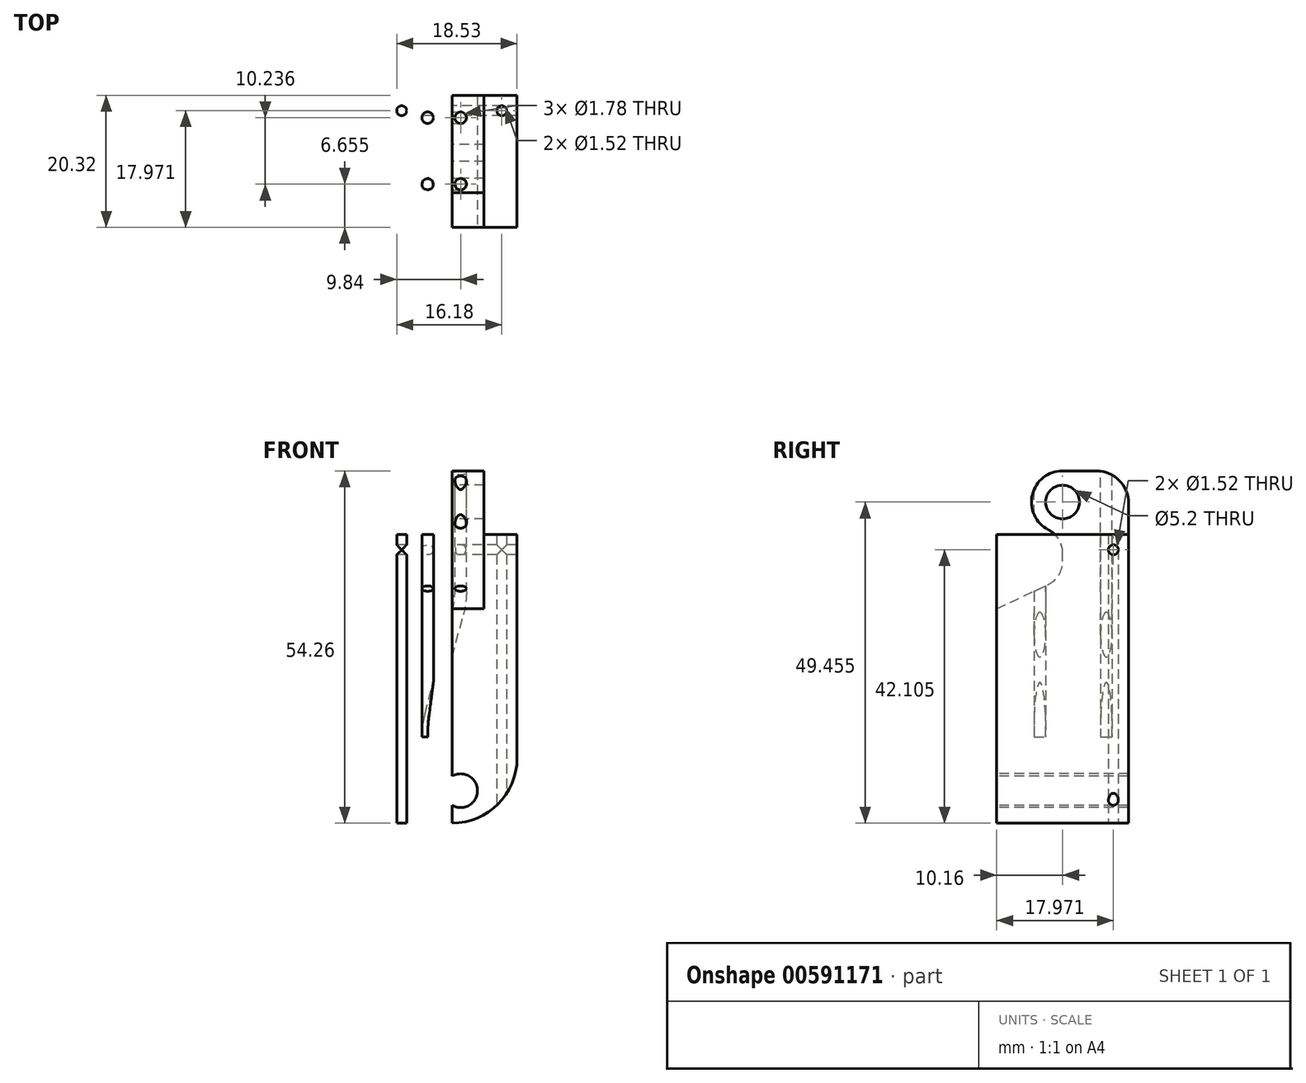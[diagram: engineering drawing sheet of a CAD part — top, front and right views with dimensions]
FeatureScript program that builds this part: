
annotation { "Feature Type Name" : "Feature", "Feature Type Description" : "" }
export const myFeature = defineFeature(function(context is Context, id is Id, definition is map)
    precondition{}
    {
        {
            var Q0;
            Q0=qCreatedBy(makeId("Front.planeOp"),FACE);
            var sketch = newSketch(context, id + "F0", { "sketchPlane" : qUnion([Q0])});
            skLineSegment(sketch, "E0.bottom", {"start": v(11.43, 22.23) * mm, "end": v(3.61, 22.23) * mm});
            skLineSegment(sketch, "E0.left", {"start": v(11.43, 22.23) * mm, "end": v(11.43, -22.22) * mm});
            skLineSegment(sketch, "E0.right", {"start": v(-11.43, 22.23) * mm, "end": v(-11.43, -22.23) * mm});
            skPoint(sketch, "E0.middle", {"position": v(0, 0) * mm});
            skLineSegment(sketch, "E1.trimOffspring", {"start": v(11.43, -22.22) * mm, "end": v(-11.43, -22.22) * mm});
            skLineSegment(sketch, "E2.bottom", {"start": v(3.61, 32.03) * mm, "end": v(-3.61, 32.03) * mm});
            skLineSegment(sketch, "E2.left", {"start": v(3.61, 32.03) * mm, "end": v(3.61, 22.23) * mm});
            skLineSegment(sketch, "E2.right", {"start": v(-3.61, 32.03) * mm, "end": v(-3.61, 22.23) * mm});
            skPoint(sketch, "E2.middle", {"position": v(0, 22.23) * mm});
            skLineSegment(sketch, "E3.trimOffspring", {"start": v(-3.61, 22.23) * mm, "end": v(-11.43, 22.23) * mm});
            skPoint(sketch, "E4.orphan", {"position": v(-3.61, 12.43) * mm});
            skPoint(sketch, "E5.orphan", {"position": v(3.61, 12.43) * mm});
            skLineSegment(sketch, "E6", {"start": v(8.7, -22.23) * mm, "end": v(8.7, 22.23) * mm});
            skSolve(sketch);
        }
        {
            var Q0;
            {var subQ1=sQuery(id+"F0.wireOp",EDGE,"E0.right");Q0=makeQuery(id+"F0.imprint","IMPRINT",FACE,{"disambiguationData":[TD([[makeQuery(id+"F0.imprint","IMPRINT",EDGE,{"derivedFrom":subQ1}),1.0]])]});}
            extrude(context, id + "F1", {"entities" : qUnion([Q0]), "depth" : 20.32 * mm, "offsetDistance" : 25.4 * mm, "symmetric" : true});
        }
        {
            var Q0;
            Q0=makeQuery(id+"F1.opExtrude","SWEPT_FACE",FACE,{"disambiguationData":[OSD([sQuery(id+"F0.wireOp",EDGE,"E0.right")])]});
            var sketch = newSketch(context, id + "F2", { "sketchPlane" : qUnion([Q0])});
            skLineSegment(sketch, "E7", {"start": v(10.16, 22.23) * mm, "end": v(-5.46, 22.23) * mm});
            skLineSegment(sketch, "E8", {"start": v(10.16, 22.23) * mm, "end": v(10.16, 10.8) * mm});
            skLineSegment(sketch, "E9", {"start": v(10.16, 10.8) * mm, "end": v(-0.57, 15.8) * mm});
            skPoint(sketch, "E10.visualSharp", {"position": v(-2.14, 14.35) * mm});
            skArc(sketch, "E10.filletArc", {"start": v(-5.46, 22.23) * mm, "mid": v(-3.7, 18.5) * mm, "end": v(-0.57, 15.8) * mm});
            skSolve(sketch);
        }
        {
            var Q0;
            Q0=makeQuery(id+"F2.imprint","IMPRINT",FACE,{"disambiguationData":[TD([[makeQuery(id+"F2.imprint","IMPRINT",EDGE,{"derivedFrom":sQuery(id+"F2.wireOp",EDGE,"E7")}),1.0]])]});
            var Q1;
            Q1=makeQuery(id+"F1.opExtrude","SWEPT_FACE",FACE,{"disambiguationData":[OSD([sQuery(id+"F0.wireOp",EDGE,"E2.right")])]});
            extrude(context, id + "F3", {"entities" : qUnion([Q0]), "operationType" : NewBodyOperationType.REMOVE, "oppositeDirection" : true, "depth" : 7.82 * mm, "endBoundEntityFace" : qUnion([Q1]), "offsetDistance" : 25.4 * mm});
        }
        {
            var Q0;
            Q0=makeQuery(id+"F3.boolean.opBoolean","MERGE",FACE,{"derivedFrom":[makeQuery(id+"F1.opExtrude","SWEPT_FACE",FACE,{"disambiguationData":[OSD([sQuery(id+"F0.wireOp",EDGE,"E2.right")])]}),makeQuery(id+"F3.opExtrude","CAP_FACE",FACE,{"disambiguationData":[OSD([sQuery(id+"F2.wireOp",EDGE,"E7"),sQuery(id+"F2.wireOp",EDGE,"E8"),sQuery(id+"F2.wireOp",EDGE,"E9"),sQuery(id+"F2.wireOp",EDGE,"E10.filletArc")])],"isStart":false})]});
            var sketch = newSketch(context, id + "F4", { "sketchPlane" : qUnion([Q0])});
            skLineSegment(sketch, "E11", {"start": v(0, 22.23) * mm, "end": v(0, 22.42) * mm});
            skCircle(sketch, "E12", {"center": v(0, 27.22) * mm, "radius": 2.6 * mm});
            skArc(sketch, "E13", {"start": v(0, 22.42) * mm, "mid": v(4.8, 27.22) * mm, "end": v(0, 32.03) * mm});
            skLineSegment(sketch, "E14", {"start": v(0, 32.03) * mm, "end": v(10.16, 32.03) * mm});
            skLineSegment(sketch, "E15", {"start": v(10.16, 32.03) * mm, "end": v(10.16, 10.8) * mm});
            skLineSegment(sketch, "E16", {"start": v(0, 22.23) * mm, "end": v(0, 15.53) * mm});
            skPoint(sketch, "E17.first.point", {"position": v(-5.46, 22.23) * mm});
            skPoint(sketch, "E17.third.point", {"position": v(12.45, 30.3) * mm});
            skLineSegment(sketch, "E18", {"start": v(0, 15.53) * mm, "end": v(10.16, 10.8) * mm});
            skSolve(sketch);
        }
        {
            var Q0;
            Q0=makeQuery(id+"F4.imprint","IMPRINT",FACE,{"disambiguationData":[TD([[makeQuery(id+"F4.imprint","IMPRINT",EDGE,{"derivedFrom":sQuery(id+"F4.wireOp",EDGE,"E12")}),1.0]])]});
            var Q1;
            Q1=makeQuery(id+"F4.imprint","IMPRINT",FACE,{"disambiguationData":[TD([[makeQuery(id+"F4.imprint","IMPRINT",EDGE,{"derivedFrom":sQuery(id+"F4.wireOp",EDGE,"E11")}),-1.0]])]});
            var Q2;
            Q2=makeQuery(id+"F1.opExtrude","SWEPT_FACE",FACE,{"disambiguationData":[OSD([sQuery(id+"F0.wireOp",EDGE,"E2.left")])]});
            extrude(context, id + "F5", {"entities" : qUnion([Q0, Q1]), "operationType" : NewBodyOperationType.REMOVE, "endBound" : BoundingType.UP_TO_SURFACE, "oppositeDirection" : true, "depth" : 25.4 * mm, "endBoundEntityFace" : qUnion([Q2]), "offsetDistance" : 25.4 * mm});
        }
        {
            var Q0;
            Q0=makeQuery(id+"F5.boolean.opBoolean","COPY",EDGE,{"derivedFrom":makeQuery(id+"F5.opExtrude","SWEPT_EDGE",EDGE,{"disambiguationData":[OSD([sQuery(id+"F4.wireOp",EDGE,"E11"),sQuery(id+"F4.wireOp",EDGE,"E13")])]})});
            var Q1;
            Q1=makeQuery(id+"F5.boolean.opBoolean","COPY",EDGE,{"derivedFrom":makeQuery(id+"F5.opExtrude","SWEPT_EDGE",EDGE,{"disambiguationData":[OSD([sQuery(id+"F4.wireOp",EDGE,"E16"),sQuery(id+"F4.wireOp",EDGE,"dM5IeoCO-8AD7-fKrw-0uPZ-bCZ9SgerwQ9h")])]})});
            fillet(context, id + "F6", {"entities" : qUnion([Q0, Q1]), "radius" : 4 * mm, "tangentPropagation" : true, "allowEdgeOverflow" : false});
        }
        {
            var Q0;
            Q0=makeQuery(id+"F1.opExtrude","CAP_EDGE",EDGE,{"disambiguationData":[OSD([sQuery(id+"F0.wireOp",EDGE,"E2.bottom")])],"isStart":true});
            fillet(context, id + "F7", {"entities" : qUnion([Q0]), "radius" : 5 * mm, "tangentPropagation" : true, "allowEdgeOverflow" : false});
        }
        {
            var Q0;
            Q0=makeQuery(id+"F1.opExtrude","SWEPT_EDGE",EDGE,{"disambiguationData":[OSD([sQuery(id+"F0.wireOp",EDGE,"E1.trimOffspring"),sQuery(id+"F0.wireOp",EDGE,"E6")])]});
            fillet(context, id + "F8", {"entities" : qUnion([Q0]), "radius" : 10 * mm, "tangentPropagation" : true, "allowEdgeOverflow" : false});
        }
        {
            var Q0;
            Q0=makeQuery(id+"F1.opExtrude","CAP_FACE",FACE,{"disambiguationData":[OSD([sQuery(id+"F0.wireOp",EDGE,"E0.bottom"),sQuery(id+"F0.wireOp",EDGE,"E0.left"),sQuery(id+"F0.wireOp",EDGE,"E0.right"),sQuery(id+"F0.wireOp",EDGE,"E1.trimOffspring"),sQuery(id+"F0.wireOp",EDGE,"E2.bottom"),sQuery(id+"F0.wireOp",EDGE,"E2.left"),sQuery(id+"F0.wireOp",EDGE,"E2.right"),sQuery(id+"F0.wireOp",EDGE,"E3.trimOffspring")])],"isStart":false});
            var sketch = newSketch(context, id + "F9", { "sketchPlane" : qUnion([Q0])});
            skCircle(sketch, "E19", {"center": v(0, -17.22) * mm, "radius": 2.6 * mm});
            skLineSegment(sketch, "E20", {"start": v(0, -17.22) * mm, "end": v(0, -22.22) * mm});
            skSolve(sketch);
        }
        {
            var Q0;
            Q0=makeQuery(id+"F9.imprint","IMPRINT",FACE,{"disambiguationData":[TD([[makeQuery(id+"F9.imprint","IMPRINT",EDGE,{"derivedFrom":sQuery(id+"F9.wireOp",EDGE,"E19")}),1.0]])]});
            extrude(context, id + "F10", {"entities" : qUnion([Q0]), "operationType" : NewBodyOperationType.REMOVE, "endBound" : BoundingType.THROUGH_ALL, "oppositeDirection" : true, "depth" : 25.4 * mm, "offsetDistance" : 25.4 * mm});
        }
        {
            var Q0;
            Q0=makeQuery(id+"F1.opExtrude","SWEPT_FACE",FACE,{"disambiguationData":[OSD([sQuery(id+"F0.wireOp",EDGE,"E0.right")])]});
            var sketch = newSketch(context, id + "F11", { "sketchPlane" : qUnion([Q0])});
            skLineSegment(sketch, "E21", {"start": v(-7.81, 22.23) * mm, "end": v(-7.81, 17.53) * mm});
            skCircle(sketch, "E22", {"center": v(-7.81, 19.88) * mm, "radius": 0.76 * mm});
            skSolve(sketch);
        }
        {
            var Q0;
            {var subQ0=sQuery(id+"F11.wireOp",EDGE,"E22");var subQ1=sQuery(id+"F11.wireOp",EDGE,"E21");var subQ2=makeQuery(id+"F11.imprint","INTERSECT",VERTEX,{"disambiguationData":[OD(0.0)],"derivedFrom":[subQ1,subQ0]});Q0=makeQuery(id+"F11.imprint","IMPRINT",FACE,{"disambiguationData":[TD([[makeQuery(id+"F11.imprint","IMPRINT",EDGE,{"disambiguationData":[TD([[subQ2,1.0]])],"derivedFrom":subQ1}),1.0]])]});}
            var Q1;
            {var subQ0=sQuery(id+"F11.wireOp",EDGE,"E22");var subQ1=sQuery(id+"F11.wireOp",EDGE,"E21");var subQ2=makeQuery(id+"F11.imprint","INTERSECT",VERTEX,{"disambiguationData":[OD(0.0)],"derivedFrom":[subQ1,subQ0]});Q1=makeQuery(id+"F11.imprint","IMPRINT",FACE,{"disambiguationData":[TD([[makeQuery(id+"F11.imprint","IMPRINT",EDGE,{"disambiguationData":[TD([[subQ2,1.0]])],"derivedFrom":subQ1}),-1.0]])]});}
            extrude(context, id + "F12", {"entities" : qUnion([Q0, Q1]), "operationType" : NewBodyOperationType.REMOVE, "endBound" : BoundingType.THROUGH_ALL, "oppositeDirection" : true, "depth" : 25.4 * mm, "offsetDistance" : 25.4 * mm});
        }
        {
            var Q0;
            Q0=makeQuery(id+"F1.opExtrude","CAP_FACE",FACE,{"disambiguationData":[OSD([sQuery(id+"F0.wireOp",EDGE,"E0.bottom"),sQuery(id+"F0.wireOp",EDGE,"E0.right"),sQuery(id+"F0.wireOp",EDGE,"E1.trimOffspring"),sQuery(id+"F0.wireOp",EDGE,"E2.bottom"),sQuery(id+"F0.wireOp",EDGE,"E2.left"),sQuery(id+"F0.wireOp",EDGE,"E2.right"),sQuery(id+"F0.wireOp",EDGE,"E3.trimOffspring"),sQuery(id+"F0.wireOp",EDGE,"E6")])],"isStart":true});
            var sketch = newSketch(context, id + "F13", { "sketchPlane" : qUnion([Q0])});
            skLineSegment(sketch, "E23", {"start": v(0, 32.03) * mm, "end": v(0, 13.38) * mm});
            skLineSegment(sketch, "E24", {"start": v(0.43, 10.09) * mm, "end": v(4.65, -5.64) * mm});
            skLineSegment(sketch, "E25", {"start": v(5.08, -8.93) * mm, "end": v(5.08, -22.22) * mm});
            skPoint(sketch, "E26.visualSharp", {"position": v(0, 11.7) * mm});
            skArc(sketch, "E26.filletArc", {"start": v(0, 13.38) * mm, "mid": v(0.1, 11.72) * mm, "end": v(0.43, 10.09) * mm});
            skPoint(sketch, "E27.visualSharp", {"position": v(5.08, -7.25) * mm});
            skArc(sketch, "E27.filletArc", {"start": v(5.08, -8.93) * mm, "mid": v(4.97, -7.27) * mm, "end": v(4.65, -5.64) * mm});
            skSolve(sketch);
        }
        {
            var Q0;
            Q0=makeQuery(id+"F1.opExtrude","SWEPT_FACE",FACE,{"disambiguationData":[OSD([sQuery(id+"F0.wireOp",EDGE,"E1.trimOffspring")])]});
            var sketch = newSketch(context, id + "F14", { "sketchPlane" : qUnion([Q0])});
            skLineSegment(sketch, "E28", {"start": v(-5.08, -10.16) * mm, "end": v(-5.08, -7.62) * mm});
            skCircle(sketch, "E29", {"center": v(-5.08, -6.73) * mm, "radius": 0.89 * mm});
            skLineSegment(sketch, "E30", {"start": v(-5.08, -7.62) * mm, "end": v(-5.08, -6.73) * mm});
            skLineSegment(sketch, "E31", {"start": v(-5.08, 10.16) * mm, "end": v(-5.08, 4.4) * mm});
            skLineSegment(sketch, "E32", {"start": v(-5.08, 4.4) * mm, "end": v(-5.08, 3.5) * mm});
            skCircle(sketch, "E33", {"center": v(-5.08, 3.5) * mm, "radius": 0.89 * mm});
            skSolve(sketch);
        }
        {
            var Q0;
            Q0=makeQuery(id+"F14.imprint","IMPRINT",FACE,{"disambiguationData":[TD([[makeQuery(id+"F14.imprint","IMPRINT",EDGE,{"derivedFrom":sQuery(id+"F14.wireOp",EDGE,"E33")}),1.0]])]});
            var Q1;
            Q1=makeQuery(id+"F14.imprint","IMPRINT",FACE,{"disambiguationData":[TD([[makeQuery(id+"F14.imprint","IMPRINT",EDGE,{"derivedFrom":sQuery(id+"F14.wireOp",EDGE,"E29")}),1.0]])]});
            var Q2;
            Q2=qConstructionFilter(qBodyType(qCreatedBy(id+"F13",EDGE),BodyType.WIRE),ConstructionObject.NO);
            sweep(context, id + "F15", {"operationType" : NewBodyOperationType.REMOVE, "profiles" : qUnion([Q0, Q1]), "path" : qUnion([Q2])});
        }
        {
            var Q0;
            Q0=makeQuery(id+"F1.opExtrude","SWEPT_FACE",FACE,{"disambiguationData":[OSD([sQuery(id+"F0.wireOp",EDGE,"E1.trimOffspring")])]});
            var sketch = newSketch(context, id + "F16", { "sketchPlane" : qUnion([Q0])});
            skLineSegment(sketch, "E34", {"start": v(8.7, -10.16) * mm, "end": v(8.7, -7.81) * mm});
            skLineSegment(sketch, "E35", {"start": v(8.7, -7.81) * mm, "end": v(6.34, -7.81) * mm});
            skCircle(sketch, "E36", {"center": v(6.34, -7.81) * mm, "radius": 0.76 * mm});
            skCircle(sketch, "E37.MirrorC", {"center": v(-9.08, -7.81) * mm, "radius": 0.76 * mm});
            skLineSegment(sketch, "E38", {"start": v(-11.43, -10.16) * mm, "end": v(-11.43, -7.81) * mm});
            skLineSegment(sketch, "E39", {"start": v(-11.43, -7.81) * mm, "end": v(-9.08, -7.81) * mm});
            skSolve(sketch);
        }
        {
            var Q0;
            Q0=makeQuery(id+"F16.imprint","IMPRINT",FACE,{"disambiguationData":[TD([[makeQuery(id+"F16.imprint","IMPRINT",EDGE,{"derivedFrom":sQuery(id+"F16.wireOp",EDGE,"E36")}),1.0]])]});
            var Q1;
            Q1=makeQuery(id+"F16.imprint","IMPRINT",FACE,{"disambiguationData":[TD([[makeQuery(id+"F16.imprint","IMPRINT",EDGE,{"derivedFrom":sQuery(id+"F16.wireOp",EDGE,"E37.MirrorC")}),-1.0]])]});
            extrude(context, id + "F17", {"entities" : qUnion([Q0, Q1]), "operationType" : NewBodyOperationType.REMOVE, "endBound" : BoundingType.THROUGH_ALL, "oppositeDirection" : true, "depth" : 25.4 * mm, "offsetDistance" : 25.4 * mm});
        }
    });
